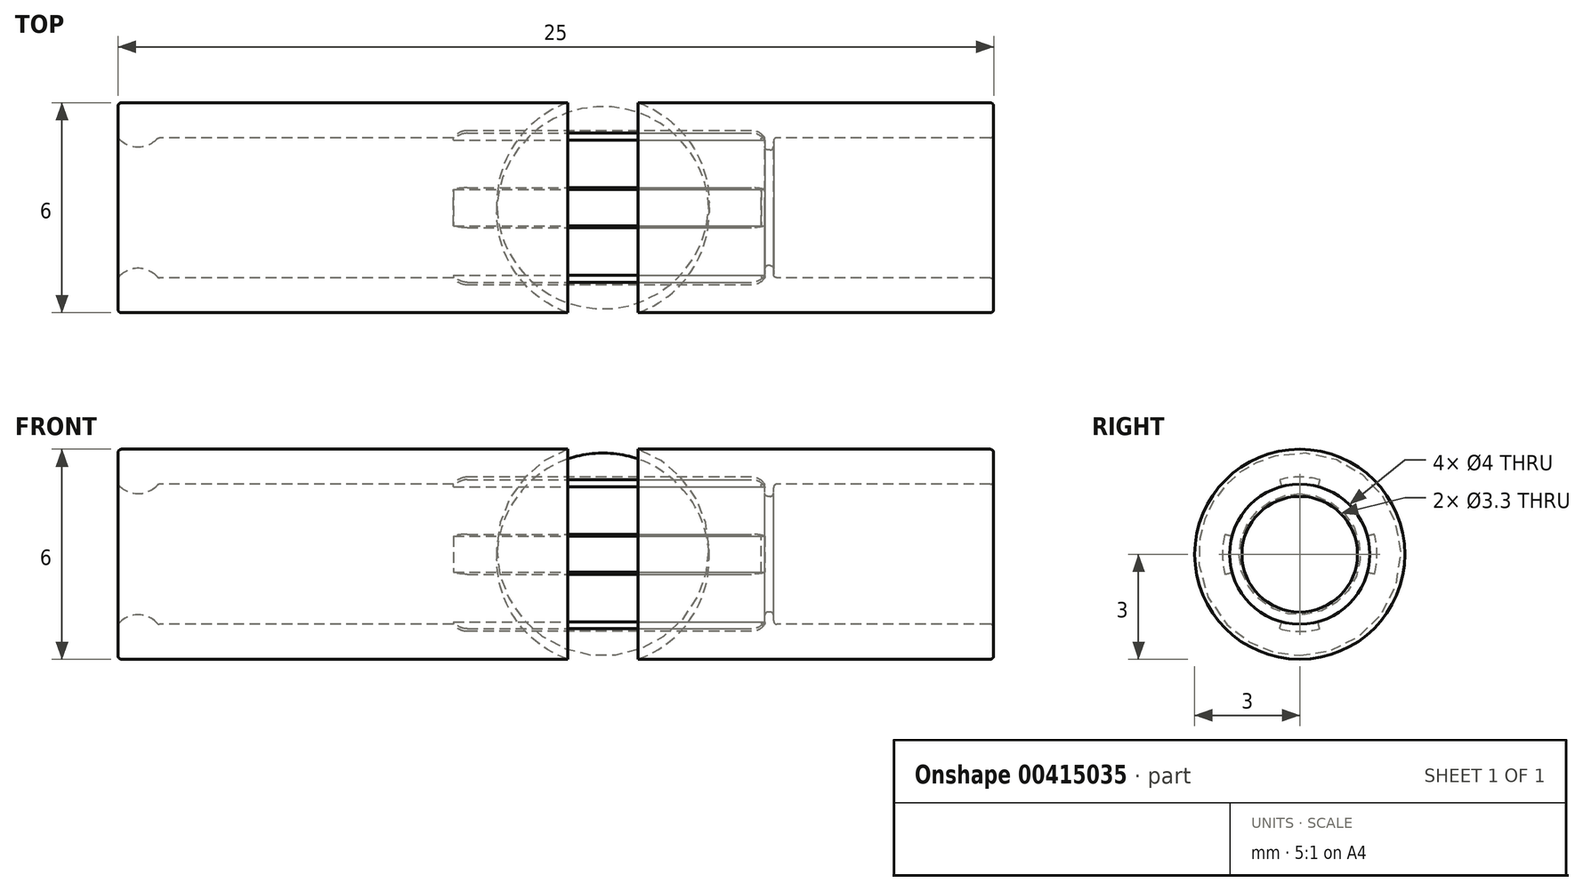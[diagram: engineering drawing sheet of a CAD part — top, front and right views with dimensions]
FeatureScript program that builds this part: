
annotation { "Feature Type Name" : "Feature", "Feature Type Description" : "" }
export const myFeature = defineFeature(function(context is Context, id is Id, definition is map)
    precondition{}
    {
        {
            var Q0;
            Q0=qCreatedBy(makeId("Front.planeOp"),FACE);
            var sketch = newSketch(context, id + "F0", { "sketchPlane" : qUnion([Q0])});
            skLineSegment(sketch, "E0.bottom", {"start": v(-10.4, 1) * mm, "end": v(14.6, 1) * mm});
            skLineSegment(sketch, "E0.top", {"start": v(-10.4, 0) * mm, "end": v(14.6, 0) * mm});
            skLineSegment(sketch, "E0.left", {"start": v(-10.4, 1) * mm, "end": v(-10.4, 0) * mm});
            skLineSegment(sketch, "E0.right", {"start": v(14.6, 1) * mm, "end": v(14.6, 0) * mm});
            skLineSegment(sketch, "E1", {"start": v(-10.4, -2) * mm, "end": v(14.6, -2) * mm});
            skLineSegment(sketch, "E2.bottom", {"start": v(8.32, 0) * mm, "end": v(8.07, 0) * mm});
            skLineSegment(sketch, "E2.top", {"start": v(8.32, -0.35) * mm, "end": v(8.07, -0.35) * mm});
            skLineSegment(sketch, "E2.left", {"start": v(8.32, 0) * mm, "end": v(8.32, -0.35) * mm});
            skLineSegment(sketch, "E2.right", {"start": v(8.07, 0) * mm, "end": v(8.07, -0.35) * mm});
            skArc(sketch, "E3", {"start": v(-10.4, 0) * mm, "mid": v(-9.82, -0.27) * mm, "end": v(-9.25, 0) * mm});
            skArc(sketch, "E4", {"start": v(4.45, 1) * mm, "mid": v(3.45, 1.17) * mm, "end": v(2.45, 1) * mm});
            skLineSegment(sketch, "E5", {"start": v(-0.42, 0.2) * mm, "end": v(7.7, 0.2) * mm});
            skArc(sketch, "E6", {"start": v(8.07, 0) * mm, "mid": v(7.9, 0.15) * mm, "end": v(7.7, 0.2) * mm});
            skArc(sketch, "E7", {"start": v(-0.42, 0.2) * mm, "mid": v(-0.64, 0.15) * mm, "end": v(-0.82, 0) * mm});
            skSolve(sketch);
        }
        {
            var Q0;
            {var subQ1=sQuery(id+"F0.wireOp",EDGE,"E0.left");Q0=makeQuery(id+"F0.imprint","IMPRINT",FACE,{"disambiguationData":[TD([[makeQuery(id+"F0.imprint","IMPRINT",EDGE,{"derivedFrom":subQ1}),1.0]])]});}
            var Q1;
            Q1=makeQuery(id+"F0.imprint","IMPRINT",FACE,{"disambiguationData":[TD([[makeQuery(id+"F0.imprint","IMPRINT",EDGE,{"derivedFrom":sQuery(id+"F0.wireOp",EDGE,"E2.top")}),-1.0]])]});
            var Q2;
            {var subQ0=sQuery(id+"F0.wireOp",EDGE,"E3");Q2=makeQuery(id+"F0.imprint","IMPRINT",FACE,{"disambiguationData":[TD([[makeQuery(id+"F0.imprint","IMPRINT",EDGE,{"derivedFrom":subQ0}),1.0]])]});}
            var Q3;
            {var subQ0=sQuery(id+"F0.wireOp",EDGE,"E4");Q3=makeQuery(id+"F0.imprint","IMPRINT",FACE,{"disambiguationData":[TD([[makeQuery(id+"F0.imprint","IMPRINT",EDGE,{"derivedFrom":subQ0}),1.0]])]});}
            var Q4;
            Q4=makeQuery(id+"F0.imprint","IMPRINT",FACE,{"disambiguationData":[TD([[makeQuery(id+"F0.imprint","IMPRINT",EDGE,{"derivedFrom":sQuery(id+"F0.wireOp",EDGE,"E5")}),-1.0]])]});
            var Q5;
            Q5=sQuery(id+"F0.wireOp",EDGE,"E1");
            revolve(context, id + "F1", {"entities" : qUnion([Q0, Q1, Q2, Q3, Q4]), "axis" : qUnion([Q5]), "revolveType" : RevolveType.FULL});
        }
        {
            var Q0;
            Q0=makeQuery(id+"F1.opRevolve","SWEPT_EDGE",EDGE,{"disambiguationData":[OSD([sQuery(id+"F0.wireOp",EDGE,"E0.top"),sQuery(id+"F0.wireOp",EDGE,"E0.left"),sQuery(id+"F0.wireOp",EDGE,"E3")])]});
            var Q1;
            Q1=makeQuery(id+"F1.opRevolve","SWEPT_EDGE",EDGE,{"disambiguationData":[OSD([sQuery(id+"F0.wireOp",EDGE,"E0.bottom"),sQuery(id+"F0.wireOp",EDGE,"E0.left")])]});
            var Q2;
            Q2=makeQuery(id+"F1.opRevolve","SWEPT_EDGE",EDGE,{"disambiguationData":[OSD([sQuery(id+"F0.wireOp",EDGE,"E0.bottom"),sQuery(id+"F0.wireOp",EDGE,"E0.right")])]});
            var Q3;
            Q3=makeQuery(id+"F1.opRevolve","SWEPT_EDGE",EDGE,{"disambiguationData":[OSD([sQuery(id+"F0.wireOp",EDGE,"E0.top"),sQuery(id+"F0.wireOp",EDGE,"E0.right")])]});
            var Q4;
            Q4=makeQuery(id+"F1.opRevolve","SWEPT_EDGE",EDGE,{"disambiguationData":[OSD([sQuery(id+"F0.wireOp",EDGE,"E0.top"),sQuery(id+"F0.wireOp",EDGE,"E2.right"),sQuery(id+"F0.wireOp",EDGE,"E6")])]});
            var Q5;
            Q5=makeQuery(id+"F1.opRevolve","SWEPT_EDGE",EDGE,{"disambiguationData":[OSD([sQuery(id+"F0.wireOp",EDGE,"E2.top"),sQuery(id+"F0.wireOp",EDGE,"E2.left")])]});
            var Q6;
            Q6=makeQuery(id+"F1.opRevolve","SWEPT_EDGE",EDGE,{"disambiguationData":[OSD([sQuery(id+"F0.wireOp",EDGE,"E0.top"),sQuery(id+"F0.wireOp",EDGE,"E2.left")])]});
            var Q7;
            Q7=makeQuery(id+"F1.opRevolve","SWEPT_EDGE",EDGE,{"disambiguationData":[OSD([sQuery(id+"F0.wireOp",EDGE,"E2.top"),sQuery(id+"F0.wireOp",EDGE,"E2.right")])]});
            var Q8;
            Q8=makeQuery(id+"F1.opRevolve","SWEPT_EDGE",EDGE,{"disambiguationData":[OSD([sQuery(id+"F0.wireOp",EDGE,"E0.top"),sQuery(id+"F0.wireOp",EDGE,"E3")])]});
            fillet(context, id + "F2", {"entities" : qUnion([Q0, Q1, Q2, Q3, Q4, Q5, Q6, Q7, Q8]), "radius" : 0.1 * mm, "tangentPropagation" : true, "allowEdgeOverflow" : false});
        }
        {
            var Q0;
            Q0=makeQuery(id+"F0.imprint","IMPRINT",FACE,{"disambiguationData":[TD([[makeQuery(id+"F0.imprint","IMPRINT",EDGE,{"derivedFrom":sQuery(id+"F0.wireOp",EDGE,"E5")}),-1.0]])]});
            var Q1;
            Q1=sQuery(id+"F0.wireOp",EDGE,"E1");
            revolve(context, id + "F3", {"entities" : qUnion([Q0]), "axis" : qUnion([Q1]), "revolveType" : RevolveType.SYMMETRIC, "angle" : 30 * degree});
        }
        {
            var Q0;
            Q0=makeQuery(id+"F3.opRevolve","SWEPT_BODY",BODY,{"disambiguationData":[OSD([sQuery(id+"F0.wireOp",EDGE,"E0.top"),sQuery(id+"F0.wireOp",EDGE,"E5"),sQuery(id+"F0.wireOp",EDGE,"E6"),sQuery(id+"F0.wireOp",EDGE,"E7")])]});
            var Q1;
            Q1=sQuery(id+"F0.wireOp",EDGE,"E1");
            circularPattern(context, id + "F4", {"operationType" : NewBodyOperationType.REMOVE, "entities" : qUnion([Q0]), "axis" : qUnion([Q1]), "angle" : 360 * degree, "instanceCount" : 4, "equalSpace" : true});
        }
    });
